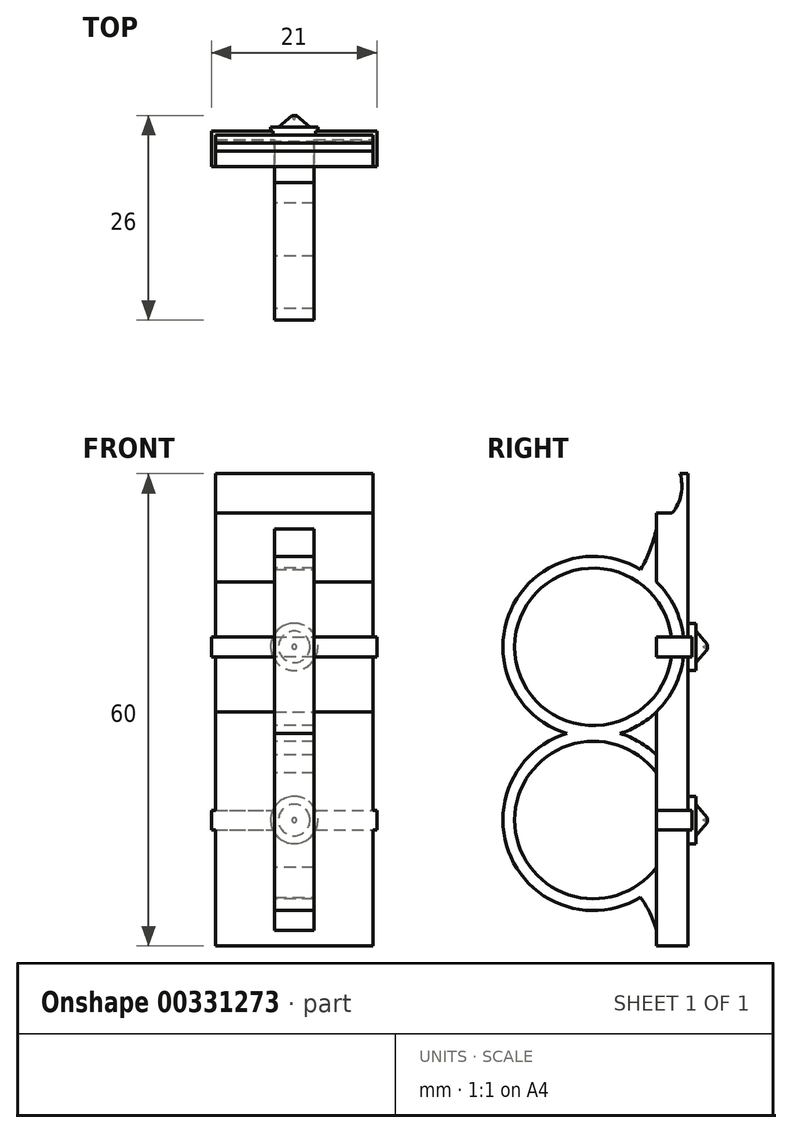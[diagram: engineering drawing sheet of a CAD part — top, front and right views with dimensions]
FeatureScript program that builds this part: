
annotation { "Feature Type Name" : "Feature", "Feature Type Description" : "" }
export const myFeature = defineFeature(function(context is Context, id is Id, definition is map)
    precondition{}
    {
        {
            var Q0;
            Q0=qCreatedBy(makeId("Right.planeOp"),FACE);
            var sketch = newSketch(context, id + "F0", { "sketchPlane" : qUnion([Q0])});
            skCircle(sketch, "E0", {"center": v(0, 0) * mm, "radius": 10 * mm});
            skCircle(sketch, "E1", {"center": v(0, 0) * mm, "radius": 11.5 * mm});
            skSolve(sketch);
        }
        {
            var Q0;
            Q0 = qSketchRegion(id + "F0", true);
            extrude(context, id + "F1", {"entities" : qUnion([Q0]), "depth" : 5 * mm});
        }
        {
            var Q0;
            Q0=makeQuery(id+"F1.opExtrude","CAP_FACE",FACE,{"disambiguationData":[OSD([sQuery(id+"F0.wireOp",EDGE,"E0"),sQuery(id+"F0.wireOp",EDGE,"E1")])],"isStart":true});
            cPlane(context, id + "F2", {"entities" : qUnion([Q0]), "cplaneType" : CPlaneType.OFFSET, "offset" : 2.5 * mm, "oppositeDirection" : true, "width" : 150 * mm, "height" : 150 * mm});
        }
        {
            var Q0;
            Q0=makeQuery(id+"F1.opExtrude","SWEPT_BODY",BODY,{"disambiguationData":[OSD([sQuery(id+"F0.wireOp",EDGE,"E0"),sQuery(id+"F0.wireOp",EDGE,"E1")])]});
            transform(context, id + "F3", {"entities" : qUnion([Q0]), "transformType" : TransformType.TRANSLATION_3D, "dx" : 0 * mm, "dy" : 0 * mm, "dz" : 22 * mm, "makeCopy" : true});
        }
        {
            var Q0;
            Q0=qCreatedBy(id+"F2.planeOp",FACE);
            var sketch = newSketch(context, id + "F4", { "sketchPlane" : qUnion([Q0])});
            skLineSegment(sketch, "E2.bottom", {"start": v(-12, -16) * mm, "end": v(-8, -16) * mm});
            skLineSegment(sketch, "E2.top", {"start": v(-12, 39) * mm, "end": v(-8, 39) * mm});
            skLineSegment(sketch, "E2.left", {"start": v(-12, -16) * mm, "end": v(-12, 39) * mm});
            skLineSegment(sketch, "E2.right", {"start": v(-8, -16) * mm, "end": v(-8, 39) * mm});
            skCircle(sketch, "E3.0", {"center": v(0, 0) * mm, "radius": 11.5 * mm});
            skCircle(sketch, "E4.0", {"center": v(0, 22) * mm, "radius": 11.5 * mm});
            skArc(sketch, "E5", {"start": v(-6, -9.81) * mm, "mid": v(-7.17, -11.82) * mm, "end": v(-8, -14) * mm});
            skArc(sketch, "E6", {"start": v(-8, 37) * mm, "mid": v(-7.2, 34.33) * mm, "end": v(-6, 31.81) * mm});
            skLineSegment(sketch, "E7", {"start": v(-12, 39) * mm, "end": v(-12, 44) * mm});
            skLineSegment(sketch, "E8", {"start": v(-12, 44) * mm, "end": v(-11, 44) * mm});
            skArc(sketch, "E9", {"start": v(-11, 44) * mm, "mid": v(-11.15, 41.37) * mm, "end": v(-10, 39) * mm});
            skSolve(sketch);
        }
        {
            var Q0;
            {var subQ0=sQuery(id+"F4.wireOp",EDGE,"E7");Q0=makeQuery(id+"F4.imprint","IMPRINT",FACE,{"disambiguationData":[TD([[makeQuery(id+"F4.imprint","IMPRINT",EDGE,{"derivedFrom":subQ0}),-1.0]])]});}
            var Q1;
            {var subQ11=sQuery(id+"F4.wireOp",EDGE,"E2.bottom");Q1=makeQuery(id+"F4.imprint","IMPRINT",FACE,{"disambiguationData":[TD([[makeQuery(id+"F4.imprint","IMPRINT",EDGE,{"derivedFrom":subQ11}),1.0]])]});}
            var Q2;
            {var subQ0=sQuery(id+"F4.wireOp",EDGE,"E4.0");var subQ1=sQuery(id+"F4.wireOp",EDGE,"E2.right");var subQ2=makeQuery(id+"F4.imprint","INTERSECT",VERTEX,{"disambiguationData":[OD(0.0)],"derivedFrom":[subQ1,subQ0]});Q2=makeQuery(id+"F4.imprint","IMPRINT",FACE,{"disambiguationData":[TD([[makeQuery(id+"F4.imprint","IMPRINT",EDGE,{"disambiguationData":[TD([[subQ2,-1.0]])],"derivedFrom":subQ1}),1.0]])]});}
            var Q3;
            {var subQ0=sQuery(id+"F4.wireOp",EDGE,"E3.0");var subQ1=sQuery(id+"F4.wireOp",EDGE,"E2.right");var subQ2=makeQuery(id+"F4.imprint","INTERSECT",VERTEX,{"disambiguationData":[OD(0.0)],"derivedFrom":[subQ1,subQ0]});Q3=makeQuery(id+"F4.imprint","IMPRINT",FACE,{"disambiguationData":[TD([[makeQuery(id+"F4.imprint","IMPRINT",EDGE,{"disambiguationData":[TD([[subQ2,-1.0]])],"derivedFrom":subQ1}),1.0]])]});}
            extrude(context, id + "F5", {"entities" : qUnion([Q0, Q1, Q2, Q3]), "operationType" : NewBodyOperationType.ADD, "depth" : 10 * mm, "hasSecondDirection" : true, "secondDirectionOppositeDirection" : true, "secondDirectionDepth" : 10 * mm});
        }
        {
            var Q0;
            Q0=makeQuery(id+"F5.opExtrude","CAP_FACE",FACE,{"disambiguationData":[OSD([sQuery(id+"F4.wireOp",EDGE,"E2.bottom"),sQuery(id+"F4.wireOp",EDGE,"E2.top"),sQuery(id+"F4.wireOp",EDGE,"E2.left"),sQuery(id+"F4.wireOp",EDGE,"E2.right"),sQuery(id+"F4.wireOp",EDGE,"E7"),sQuery(id+"F4.wireOp",EDGE,"E8"),sQuery(id+"F4.wireOp",EDGE,"E9")])],"isStart":false});
            var sketch = newSketch(context, id + "F6", { "sketchPlane" : qUnion([Q0])});
            skArc(sketch, "E10.0", {"start": v(-8, 6) * mm, "mid": v(10, 0) * mm, "end": v(-8, -6) * mm});
            skArc(sketch, "E11.0", {"start": v(-8, 28) * mm, "mid": v(10, 22) * mm, "end": v(-8, 16) * mm});
            skLineSegment(sketch, "E12.bottom", {"start": v(-12.5, 1.25) * mm, "end": v(-8, 1.25) * mm});
            skLineSegment(sketch, "E12.top", {"start": v(-12.5, -1.25) * mm, "end": v(-8, -1.25) * mm});
            skLineSegment(sketch, "E12.left", {"start": v(-12.5, -1.25) * mm, "end": v(-12.5, 1.25) * mm});
            skLineSegment(sketch, "E12.right", {"start": v(-8, -1.25) * mm, "end": v(-8, 1.25) * mm});
            skLineSegment(sketch, "E13.bottom", {"start": v(-12.5, 20.75) * mm, "end": v(-8, 20.75) * mm});
            skLineSegment(sketch, "E13.top", {"start": v(-12.5, 23.25) * mm, "end": v(-8, 23.25) * mm});
            skLineSegment(sketch, "E13.left", {"start": v(-12.5, 20.75) * mm, "end": v(-12.5, 23.25) * mm});
            skLineSegment(sketch, "E13.right", {"start": v(-8, 20.75) * mm, "end": v(-8, 23.25) * mm});
            skPoint(sketch, "E14", {"position": v(-8, 0) * mm});
            skPoint(sketch, "E15", {"position": v(-8, 22) * mm});
            skSolve(sketch);
        }
        {
            var Q0;
            Q0 = qSketchRegion(id + "F6", true);
            extrude(context, id + "F7", {"entities" : qUnion([Q0]), "operationType" : NewBodyOperationType.ADD, "depth" : .5 * mm, "hasSecondDirection" : true, "secondDirectionOppositeDirection" : true, "secondDirectionDepth" : 20.5 * mm});
        }
        {
            var Q0;
            Q0=makeQuery(id+"F7.opExtrude","SWEPT_FACE",FACE,{"disambiguationData":[OSD([sQuery(id+"F6.wireOp",EDGE,"E13.left")])]});
            var sketch = newSketch(context, id + "F8", { "sketchPlane" : qUnion([Q0])});
            skCircle(sketch, "E16", {"center": v(-2.5, 22) * mm, "radius": 3 * mm});
            skPoint(sketch, "E16.centerSnap0", {"position": v(-2.5, 20.75) * mm});
            skPoint(sketch, "E16.centerSnap1", {"position": v(8, 22) * mm});
            skLineSegment(sketch, "E17", {"start": v(-0.17, 11) * mm, "end": v(-6.27, 11) * mm});
            skCircle(sketch, "E18.MirrorC", {"center": v(-2.5, 0) * mm, "radius": 3 * mm});
            skPoint(sketch, "E19.MirrorP", {"position": v(-2.5, 1.25) * mm});
            skPoint(sketch, "E20.MirrorP", {"position": v(8, 0) * mm});
            skSolve(sketch);
        }
        {
            var Q0;
            Q0 = qSketchRegion(id + "F8", true);
            var Q1;
            {var subQ0=sQuery(id+"F4.wireOp",EDGE,"E2.bottom");var subQ3=sQuery(id+"F4.wireOp",EDGE,"E7");var subQ5=sQuery(id+"F4.wireOp",EDGE,"E2.left");Q1=makeQuery(id+"F7.boolean.opBoolean","SPLIT",FACE,{"disambiguationData":[TD([makeQuery(id+"F5.opExtrude","SWEPT_FACE",FACE,{"disambiguationData":[OSD([subQ0])]})])],"derivedFrom":makeQuery(id+"F5.opExtrude","SWEPT_FACE",FACE,{"disambiguationData":[OSD([subQ5,subQ3])]})});}
            extrude(context, id + "F9", {"entities" : qUnion([Q0]), "operationType" : NewBodyOperationType.ADD, "depth" : .5 * mm, "hasSecondDirection" : true, "secondDirectionBound" : SecondDirectionBoundingType.UP_TO_SURFACE, "secondDirectionOppositeDirection" : true, "secondDirectionBoundEntityFace" : qUnion([Q1]), "secondDirectionDepth" : 25 * mm});
        }
        {
            var Q0;
            Q0=qCreatedBy(id+"F2.planeOp",FACE);
            var sketch = newSketch(context, id + "F10", { "sketchPlane" : qUnion([Q0])});
            skLineSegment(sketch, "E21.0", {"start": v(-13, 3) * mm, "end": v(-13, -3) * mm});
            skLineSegment(sketch, "E22", {"start": v(-13, 0) * mm, "end": v(-14.5, 0) * mm});
            skLineSegment(sketch, "E23", {"start": v(-13, -2) * mm, "end": v(-14.5, -0.3) * mm});
            skLineSegment(sketch, "E24", {"start": v(-14.5, -0.3) * mm, "end": v(-13.9, 0) * mm});
            skLineSegment(sketch, "E25", {"start": v(-10.5, 19) * mm, "end": v(-11.5, 19) * mm});
            skLineSegment(sketch, "E26", {"start": v(-11.5, 3) * mm, "end": v(-10.5, 3) * mm});
            skLineSegment(sketch, "E27", {"start": v(-14.34, 11) * mm, "end": v(-11.5, 11) * mm});
            skLineSegment(sketch, "E28.MirrorCS", {"start": v(-14.5, 22.3) * mm, "end": v(-13.9, 22) * mm});
            skLineSegment(sketch, "E29.MirrorCS", {"start": v(-13, 22) * mm, "end": v(-14.5, 22) * mm});
            skLineSegment(sketch, "E30.MirrorCS", {"start": v(-13, 24) * mm, "end": v(-14.5, 22.3) * mm});
            skLineSegment(sketch, "E31", {"start": v(-13, 22) * mm, "end": v(-13, 24) * mm});
            skSolve(sketch);
        }
        {
            var Q0;
            {var subQ3=sQuery(id+"F10.wireOp",EDGE,"E23");Q0=makeQuery(id+"F10.imprint","IMPRINT",FACE,{"disambiguationData":[TD([[makeQuery(id+"F10.imprint","IMPRINT",EDGE,{"derivedFrom":subQ3}),-1.0]])]});}
            var Q1;
            Q1=sQuery(id+"F10.wireOp",EDGE,"E22");
            revolve(context, id + "F11", {"operationType" : NewBodyOperationType.ADD, "entities" : qUnion([Q0]), "axis" : qUnion([Q1]), "revolveType" : RevolveType.FULL});
        }
        {
            var Q0;
            {var subQ0=sQuery(id+"F10.wireOp",EDGE,"E28.MirrorCS");Q0=makeQuery(id+"F10.imprint","IMPRINT",FACE,{"disambiguationData":[TD([[makeQuery(id+"F10.imprint","IMPRINT",EDGE,{"derivedFrom":subQ0}),1.0]])]});}
            var Q1;
            Q1=sQuery(id+"F10.wireOp",EDGE,"E29.MirrorCS");
            revolve(context, id + "F12", {"operationType" : NewBodyOperationType.ADD, "entities" : qUnion([Q0]), "axis" : qUnion([Q1]), "revolveType" : RevolveType.FULL});
        }
        {
            var Q0;
            {var subQ0=sQuery(id+"F4.wireOp",EDGE,"E6");Q0=makeQuery(id+"F4.imprint","IMPRINT",FACE,{"disambiguationData":[TD([[makeQuery(id+"F4.imprint","IMPRINT",EDGE,{"derivedFrom":subQ0}),-1.0]])]});}
            var Q1;
            {var subQ0=sQuery(id+"F4.wireOp",EDGE,"E5");Q1=makeQuery(id+"F4.imprint","IMPRINT",FACE,{"disambiguationData":[TD([[makeQuery(id+"F4.imprint","IMPRINT",EDGE,{"derivedFrom":subQ0}),-1.0]])]});}
            extrude(context, id + "F13", {"entities" : qUnion([Q0, Q1]), "operationType" : NewBodyOperationType.ADD, "depth" : 2.5 * mm, "hasSecondDirection" : true, "secondDirectionOppositeDirection" : true, "secondDirectionDepth" : 2.5 * mm});
        }
    });
